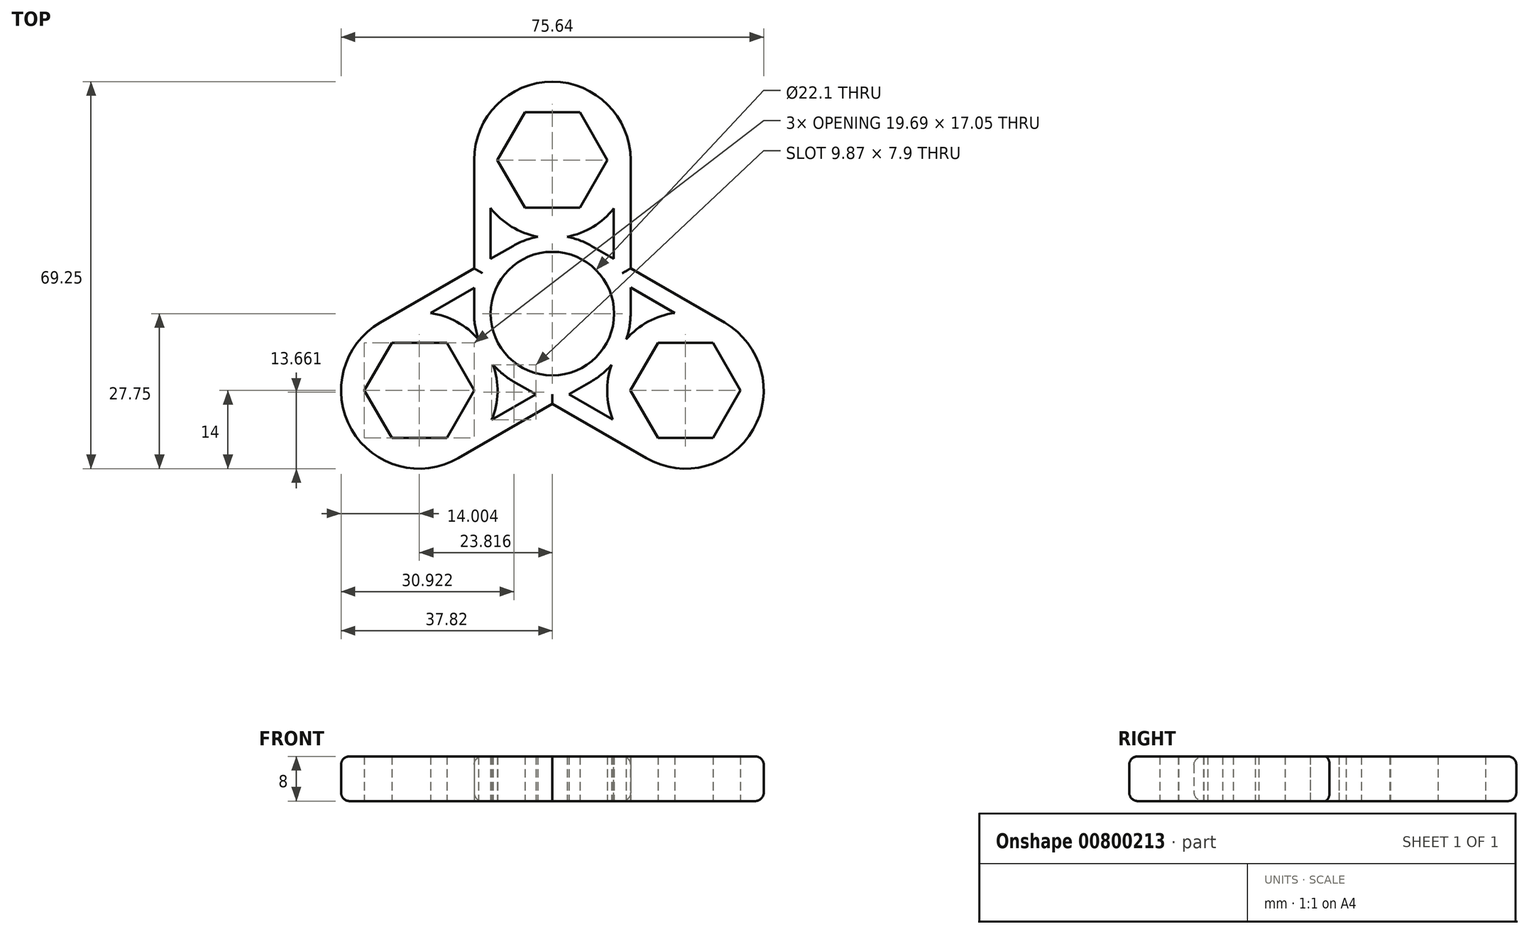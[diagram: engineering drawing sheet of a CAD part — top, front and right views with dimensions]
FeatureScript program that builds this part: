
annotation { "Feature Type Name" : "Feature", "Feature Type Description" : "" }
export const myFeature = defineFeature(function(context is Context, id is Id, definition is map)
    precondition{}
    {
        {
            var Q0;
            Q0=qCreatedBy(makeId("Top.planeOp"),FACE);
            var sketch = newSketch(context, id + "F0", { "sketchPlane" : qUnion([Q0])});
            skCircle(sketch, "E0", {"center": v(0, 0) * mm, "radius": 11.05 * mm});
            skLineSegment(sketch, "E1", {"start": v(0, 0) * mm, "end": v(0, 27.5) * mm, "construction": true});
            skCircle(sketch, "E2.cCircle", {"center": v(0, 27.5) * mm, "radius": 8.53 * mm, "construction": true});
            skLineSegment(sketch, "E2.0", {"start": v(-4.92, 36.03) * mm, "end": v(4.92, 36.03) * mm});
            skLineSegment(sketch, "E2.1", {"start": v(4.92, 36.03) * mm, "end": v(9.84, 27.5) * mm});
            skLineSegment(sketch, "E2.2", {"start": v(9.84, 27.5) * mm, "end": v(4.92, 18.98) * mm});
            skLineSegment(sketch, "E2.3", {"start": v(4.92, 18.98) * mm, "end": v(-4.92, 18.98) * mm});
            skLineSegment(sketch, "E2.4", {"start": v(-4.92, 18.98) * mm, "end": v(-9.84, 27.5) * mm});
            skLineSegment(sketch, "E2.5", {"start": v(-9.84, 27.5) * mm, "end": v(-4.92, 36.03) * mm});
            skPoint(sketch, "E2.0.midPoint", {"position": v(0, 36.03) * mm});
            skArc(sketch, "E3", {"start": v(-14, 0) * mm, "mid": v(0, -14) * mm, "end": v(14, 0) * mm});
            skArc(sketch, "E4", {"start": v(14, 27.5) * mm, "mid": v(0, 41.5) * mm, "end": v(-14, 27.5) * mm});
            skLineSegment(sketch, "E5.left", {"start": v(14, 0) * mm, "end": v(14, 27.5) * mm});
            skLineSegment(sketch, "E5.right", {"start": v(11, 8.66) * mm, "end": v(11, 18.84) * mm});
            skLineSegment(sketch, "E6.left", {"start": v(-14, 27.5) * mm, "end": v(-14, 0) * mm});
            skLineSegment(sketch, "E6.right", {"start": v(-11.05, 18.9) * mm, "end": v(-11.05, 8.6) * mm});
            skArc(sketch, "E7.trimOffspring", {"start": v(11, 8.66) * mm, "mid": v(7.28, 11.96) * mm, "end": v(2.63, 13.75) * mm});
            skPoint(sketch, "E6.top.end.orphan", {"position": v(-11.05, 0) * mm});
            skArc(sketch, "E8.trimOffspring", {"start": v(-11.05, 18.9) * mm, "mid": v(-7.31, 15.56) * mm, "end": v(-2.63, 13.75) * mm});
            skArc(sketch, "E9.trimOffspring", {"start": v(-2.63, 13.75) * mm, "mid": v(-7.31, 11.94) * mm, "end": v(-11.05, 8.6) * mm});
            skArc(sketch, "E10.trimOffspring", {"start": v(2.63, 13.75) * mm, "mid": v(7.28, 15.54) * mm, "end": v(11, 18.84) * mm});
            skSolve(sketch);
        }
        {
            var Q0;
            Q0=makeQuery(id+"F0.imprint","IMPRINT",FACE,{"disambiguationData":[TD([[makeQuery(id+"F0.imprint","IMPRINT",EDGE,{"derivedFrom":sQuery(id+"F0.wireOp",EDGE,"E0")}),-1.0]])]});
            extrude(context, id + "F1", {"entities" : qUnion([Q0]), "endBound" : BoundingType.SYMMETRIC, "depth" : 8 * mm, "offsetDistance" : 25 * mm});
        }
        {
            var Q0;
            Q0=makeQuery(id+"F1.opExtrude","SWEPT_BODY",BODY,{"disambiguationData":[OSD([sQuery(id+"F0.wireOp",EDGE,"E0"),sQuery(id+"F0.wireOp",EDGE,"E2.0"),sQuery(id+"F0.wireOp",EDGE,"E2.1"),sQuery(id+"F0.wireOp",EDGE,"E2.2"),sQuery(id+"F0.wireOp",EDGE,"E2.3"),sQuery(id+"F0.wireOp",EDGE,"E2.4"),sQuery(id+"F0.wireOp",EDGE,"E2.5"),sQuery(id+"F0.wireOp",EDGE,"E3"),sQuery(id+"F0.wireOp",EDGE,"E4"),sQuery(id+"F0.wireOp",EDGE,"E5.left"),sQuery(id+"F0.wireOp",EDGE,"E5.right"),sQuery(id+"F0.wireOp",EDGE,"E6.left"),sQuery(id+"F0.wireOp",EDGE,"E6.right"),sQuery(id+"F0.wireOp",EDGE,"E7.trimOffspring"),sQuery(id+"F0.wireOp",EDGE,"E8.trimOffspring"),sQuery(id+"F0.wireOp",EDGE,"E9.trimOffspring"),sQuery(id+"F0.wireOp",EDGE,"E10.trimOffspring")])]});
            var Q1;
            Q1=makeQuery(id+"F1.opExtrude","CAP_EDGE",EDGE,{"disambiguationData":[OSD([sQuery(id+"F0.wireOp",EDGE,"E0")])],"isStart":false});
            circularPattern(context, id + "F2", {"operationType" : NewBodyOperationType.ADD, "entities" : qUnion([Q0]), "axis" : qUnion([Q1]), "angle" : 360 * degree, "instanceCount" : 3, "equalSpace" : true});
        }
        {
            var Q0;
            Q0=makeQuery(id+"F1.opExtrude","SWEPT_FACE",FACE,{"disambiguationData":[OSD([sQuery(id+"F0.wireOp",EDGE,"E4")])]});
            var Q1;
            Q1=makeQuery(id+"F2.opPattern","COPY",FACE,{"derivedFrom":makeQuery(id+"F1.opExtrude","SWEPT_FACE",FACE,{"disambiguationData":[OSD([sQuery(id+"F0.wireOp",EDGE,"E4")])]}),"instanceName":"2"});
            var Q2;
            Q2=makeQuery(id+"F2.opPattern","COPY",FACE,{"derivedFrom":makeQuery(id+"F1.opExtrude","SWEPT_FACE",FACE,{"disambiguationData":[OSD([sQuery(id+"F0.wireOp",EDGE,"E4")])]}),"instanceName":"1"});
            fillet(context, id + "F3", {"entities" : qUnion([Q0, Q1, Q2]), "radius" : 1.5 * mm, "tangentPropagation" : true, "allowEdgeOverflow" : false});
        }
    });
